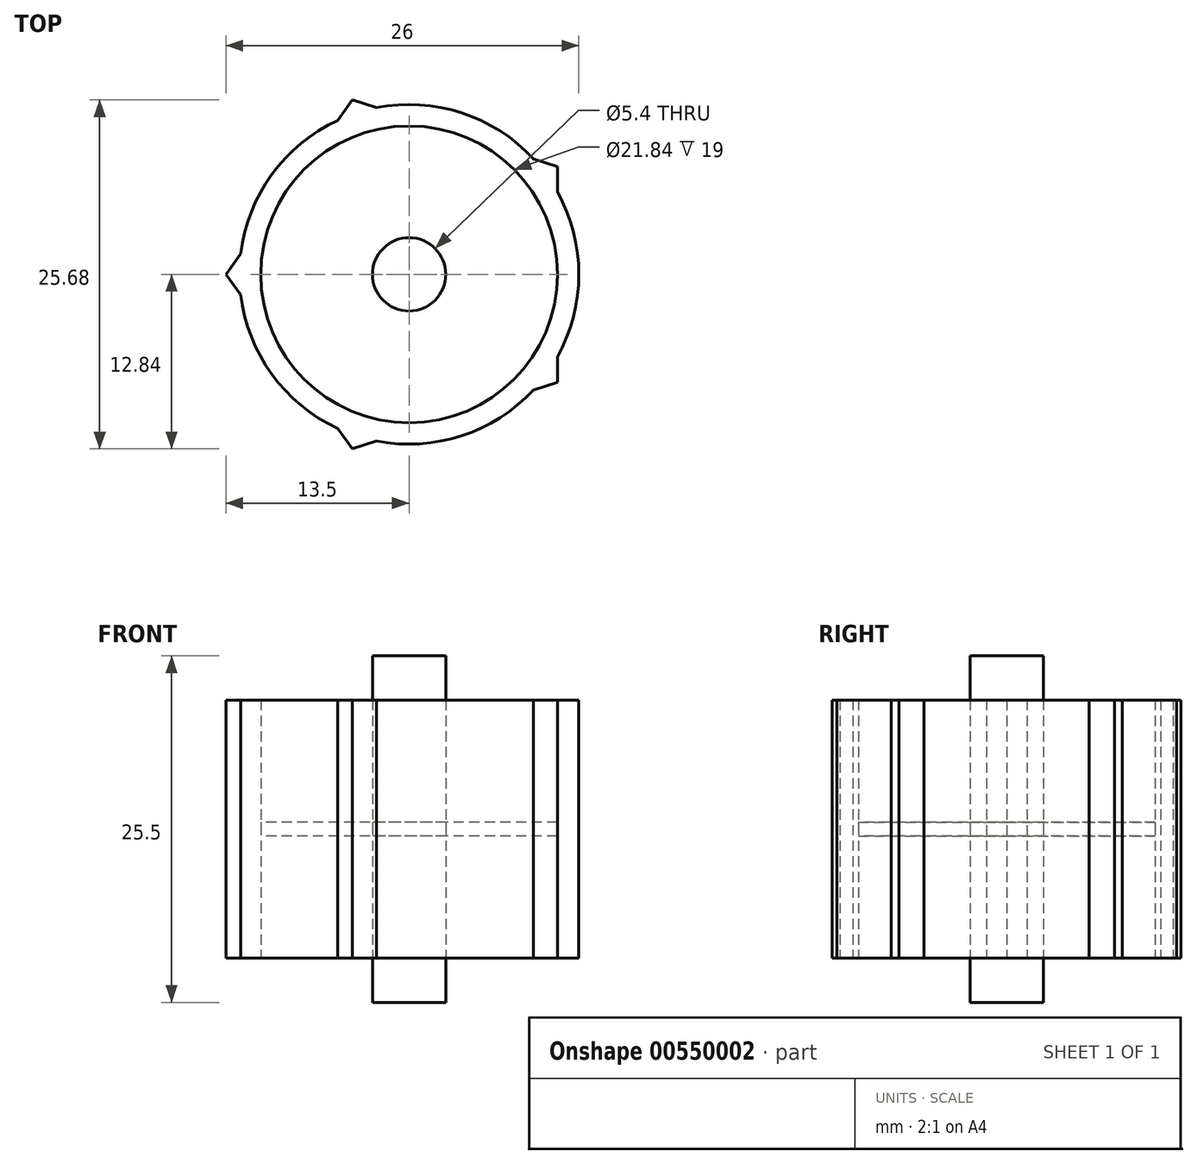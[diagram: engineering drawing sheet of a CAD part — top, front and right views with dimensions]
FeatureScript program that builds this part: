
annotation { "Feature Type Name" : "Feature", "Feature Type Description" : "" }
export const myFeature = defineFeature(function(context is Context, id is Id, definition is map)
    precondition{}
    {
        {
            var Q0;
            Q0=qCreatedBy(makeId("Top.planeOp"),FACE);
            var sketch = newSketch(context, id + "F0", { "sketchPlane" : qUnion([Q0])});
            skCircle(sketch, "E0", {"center": v(0, 0) * mm, "radius": 13.5 * mm, "construction": true});
            skCircle(sketch, "E1.cCircle", {"center": v(0, 0) * mm, "radius": 10.92 * mm, "construction": true});
            skLineSegment(sketch, "E1.0", {"start": v(10.92, 7.94) * mm, "end": v(10.92, -7.94) * mm});
            skLineSegment(sketch, "E1.1", {"start": v(10.92, -7.94) * mm, "end": v(-4.17, -12.84) * mm});
            skLineSegment(sketch, "E1.2", {"start": v(-4.17, -12.84) * mm, "end": v(-13.5, 0) * mm});
            skLineSegment(sketch, "E1.3", {"start": v(-13.5, 0) * mm, "end": v(-4.17, 12.84) * mm});
            skLineSegment(sketch, "E1.4", {"start": v(-4.17, 12.84) * mm, "end": v(10.92, 7.94) * mm});
            skPoint(sketch, "E1.0.midPoint", {"position": v(10.92, 0) * mm});
            skCircle(sketch, "E2.0", {"center": v(0, 0) * mm, "radius": 12.5 * mm});
            skCircle(sketch, "E3", {"center": v(0, 0) * mm, "radius": 2.7 * mm});
            skCircle(sketch, "E4", {"center": v(0, 0) * mm, "radius": 10.92 * mm});
            skSolve(sketch);
        }
        {
            var Q0;
            Q0 = qSketchRegion(id + "F0", true);
            var Q1;
            Q1=makeQuery(id+"F0.imprint","IMPRINT",FACE,{"disambiguationData":[TD([[makeQuery(id+"F0.imprint","IMPRINT",EDGE,{"derivedFrom":sQuery(id+"F0.wireOp",EDGE,"E3")}),1.0]])]});
            extrude(context, id + "F1", {"entities" : qUnion([Q0, Q1]), "endBound" : BoundingType.SYMMETRIC, "depth" : 19 * mm, "offsetDistance" : 25 * mm});
        }
        {
            var Q0;
            Q0=makeQuery(id+"F0.imprint","IMPRINT",FACE,{"disambiguationData":[TD([[makeQuery(id+"F0.imprint","IMPRINT",EDGE,{"derivedFrom":sQuery(id+"F0.wireOp",EDGE,"E3")}),1.0]])]});
            extrude(context, id + "F2", {"entities" : qUnion([Q0]), "operationType" : NewBodyOperationType.ADD, "endBound" : BoundingType.SYMMETRIC, "depth" : 25.5 * mm, "offsetDistance" : 25 * mm});
        }
        {
            var Q0;
            Q0=makeQuery(id+"F0.imprint","IMPRINT",FACE,{"disambiguationData":[TD([[makeQuery(id+"F0.imprint","IMPRINT",EDGE,{"derivedFrom":sQuery(id+"F0.wireOp",EDGE,"E3")}),-1.0]])]});
            extrude(context, id + "F3", {"entities" : qUnion([Q0]), "endBound" : BoundingType.SYMMETRIC, "depth" : 1 * mm, "offsetDistance" : 25 * mm});
        }
    });
